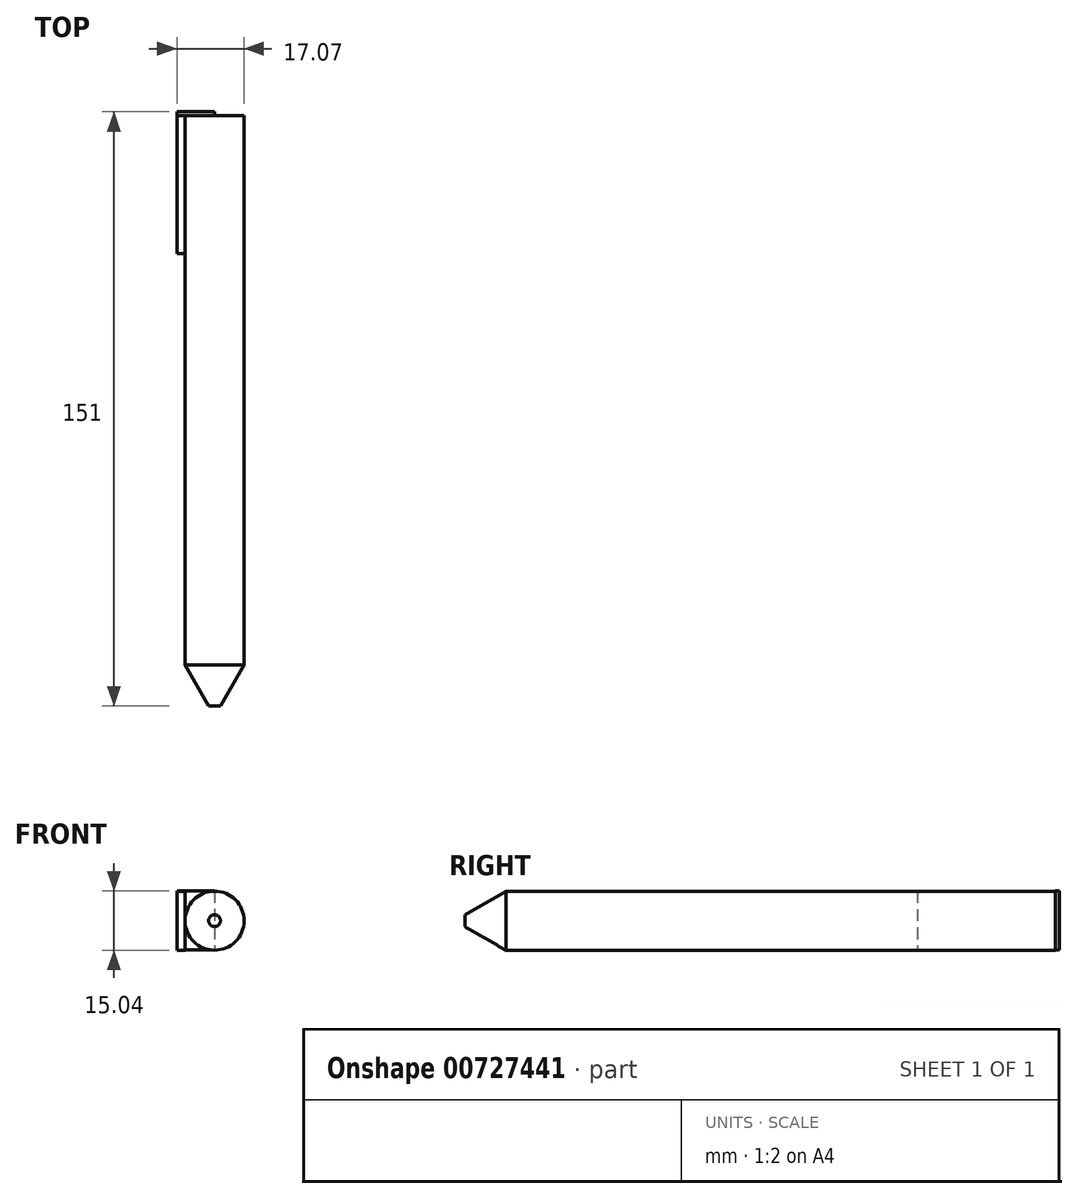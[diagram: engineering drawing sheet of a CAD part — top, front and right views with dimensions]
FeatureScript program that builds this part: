
annotation { "Feature Type Name" : "Feature", "Feature Type Description" : "" }
export const myFeature = defineFeature(function(context is Context, id is Id, definition is map)
    precondition{}
    {
        {
            var Q0;
            Q0=qCreatedBy(makeId("Front.planeOp"),FACE);
            var sketch = newSketch(context, id + "F0", { "sketchPlane" : qUnion([Q0])});
            skCircle(sketch, "E0", {"center": v(0, 0) * mm, "radius": 7.5 * mm});
            skSolve(sketch);
        }
        {
            var Q0;
            Q0 = qSketchRegion(id + "F0", true);
            extrude(context, id + "F1", {"entities" : qUnion([Q0]), "depth" : 150 * mm, "offsetDistance" : 25.4 * mm});
        }
        {
            var Q0;
            Q0=makeQuery(id+"F1.opExtrude","CAP_EDGE",EDGE,{"disambiguationData":[OSD([sQuery(id+"F0.wireOp",EDGE,"E0")])],"isStart":false});
            chamfer(context, id + "F2", {"entities" : qUnion([Q0]), "chamferType" : ChamferType.OFFSET_ANGLE, "width" : 6 * mm, "oppositeDirection" : false, "angle" : 60 * degree, "tangentPropagation" : true});
        }
        {
            var Q0;
            Q0=qCreatedBy(makeId("Front.planeOp"),FACE);
            var sketch = newSketch(context, id + "F3", { "sketchPlane" : qUnion([Q0])});
            skLineSegment(sketch, "E1", {"start": v(0, 7.5) * mm, "end": v(-7.5, 7.5) * mm});
            skLineSegment(sketch, "E2", {"start": v(0, -7.5) * mm, "end": v(-9.57, -7.5) * mm});
            skLineSegment(sketch, "E3.bottom", {"start": v(-7.5, 7.5) * mm, "end": v(-9.57, 7.5) * mm});
            skLineSegment(sketch, "E3.top", {"start": v(-7.5, -7.5) * mm, "end": v(-9.57, -7.5) * mm});
            skLineSegment(sketch, "E3.left", {"start": v(-7.5, 7.5) * mm, "end": v(-7.5, -7.5) * mm});
            skLineSegment(sketch, "E3.right", {"start": v(-9.57, 7.5) * mm, "end": v(-9.57, -7.5) * mm});
            skSolve(sketch);
        }
        {
            var Q0;
            Q0 = qSketchRegion(id + "F3", true);
            extrude(context, id + "F4", {"entities" : qUnion([Q0]), "operationType" : NewBodyOperationType.ADD, "depth" : 35 * mm, "offsetDistance" : 25.4 * mm});
        }
        {
            var Q0;
            Q0=qCreatedBy(makeId("Front.planeOp"),FACE);
            var sketch = newSketch(context, id + "F5", { "sketchPlane" : qUnion([Q0])});
            skLineSegment(sketch, "E4.bottom", {"start": v(0, 7.54) * mm, "end": v(-9.55, 7.54) * mm});
            skLineSegment(sketch, "E4.top", {"start": v(0, -7.46) * mm, "end": v(-9.55, -7.46) * mm});
            skLineSegment(sketch, "E4.left", {"start": v(0, 7.54) * mm, "end": v(0, -7.46) * mm});
            skLineSegment(sketch, "E4.right", {"start": v(-9.55, 7.54) * mm, "end": v(-9.55, -7.46) * mm});
            skSolve(sketch);
        }
        {
            var Q0;
            Q0=makeQuery(id+"F5.imprint","IMPRINT",FACE,{"disambiguationData":[TD([[makeQuery(id+"F5.imprint","IMPRINT",EDGE,{"derivedFrom":sQuery(id+"F5.wireOp",EDGE,"E4.bottom")}),1.0]])]});
            extrude(context, id + "F6", {"entities" : qUnion([Q0]), "oppositeDirection" : true, "depth" : 1 * mm, "offsetDistance" : 25.4 * mm});
        }
    });
